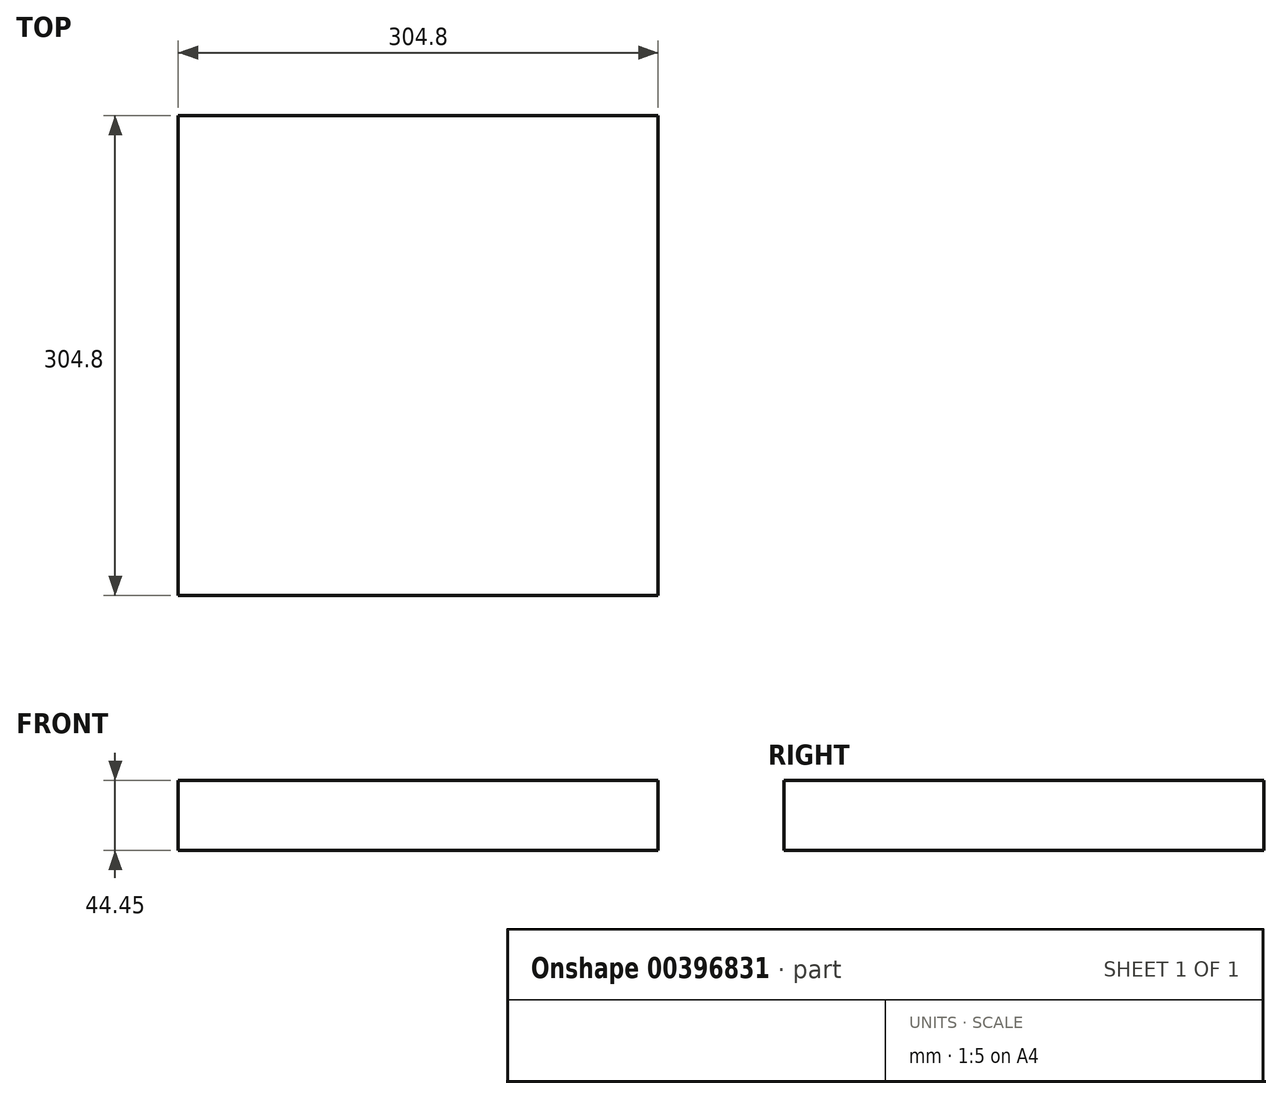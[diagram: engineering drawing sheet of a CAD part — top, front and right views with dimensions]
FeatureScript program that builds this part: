
annotation { "Feature Type Name" : "Feature", "Feature Type Description" : "" }
export const myFeature = defineFeature(function(context is Context, id is Id, definition is map)
    precondition{}
    {
        {
            var Q0;
            Q0=qCreatedBy(makeId("Top.planeOp"),FACE);
            var sketch = newSketch(context, id + "F0", { "sketchPlane" : qUnion([Q0])});
            skLineSegment(sketch, "E0.bottom", {"start": v(-152.4, 152.4) * mm, "end": v(152.4, 152.4) * mm});
            skLineSegment(sketch, "E0.top", {"start": v(-152.4, -152.4) * mm, "end": v(152.4, -152.4) * mm});
            skLineSegment(sketch, "E0.left", {"start": v(-152.4, 152.4) * mm, "end": v(-152.4, -152.4) * mm});
            skLineSegment(sketch, "E0.right", {"start": v(152.4, 152.4) * mm, "end": v(152.4, -152.4) * mm});
            skPoint(sketch, "E0.middle", {"position": v(0, 0) * mm});
            skSolve(sketch);
        }
        {
            var Q0;
            Q0=makeQuery(id+"F0.imprint","IMPRINT",FACE,{"disambiguationData":[TD([[makeQuery(id+"F0.imprint","IMPRINT",EDGE,{"derivedFrom":sQuery(id+"F0.wireOp",EDGE,"E0.bottom")}),-1.0]])]});
            extrude(context, id + "F1", {"entities" : qUnion([Q0]), "depth" : 44.45 * mm});
        }
    });
